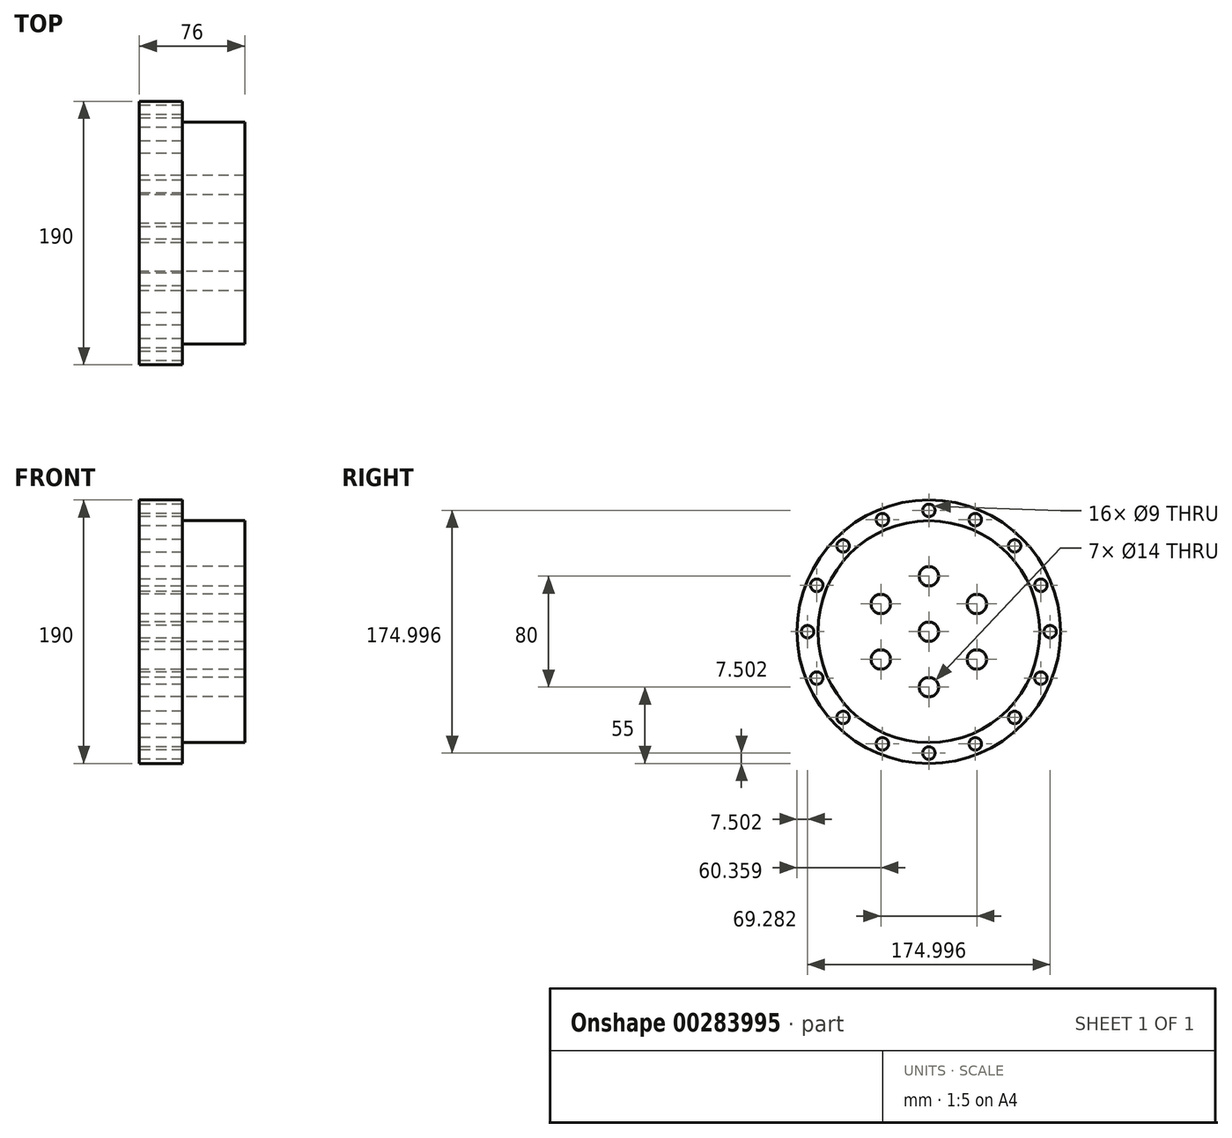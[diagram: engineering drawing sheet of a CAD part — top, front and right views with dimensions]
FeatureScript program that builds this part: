
annotation { "Feature Type Name" : "Feature", "Feature Type Description" : "" }
export const myFeature = defineFeature(function(context is Context, id is Id, definition is map)
    precondition{}
    {
        {
            var Q0;
            Q0=qCreatedBy(makeId("Right.planeOp"),FACE);
            var sketch = newSketch(context, id + "F0", { "sketchPlane" : qUnion([Q0])});
            skCircle(sketch, "E0", {"center": v(0, 0) * mm, "radius": 95 * mm});
            skCircle(sketch, "E1", {"center": v(0, 0) * mm, "radius": 80 * mm});
            skCircle(sketch, "E2", {"center": v(0, 0) * mm, "radius": 7 * mm});
            skCircle(sketch, "E3", {"center": v(0, 40) * mm, "radius": 7 * mm});
            skCircle(sketch, "E4.1.0", {"center": v(-34.64, 20) * mm, "radius": 7 * mm});
            skCircle(sketch, "E4.2.0", {"center": v(-34.64, -20) * mm, "radius": 7 * mm});
            skCircle(sketch, "E4.3.0", {"center": v(0, -40) * mm, "radius": 7 * mm});
            skCircle(sketch, "E4.4.0", {"center": v(34.64, -20) * mm, "radius": 7 * mm});
            skCircle(sketch, "E4.5.0", {"center": v(34.64, 20) * mm, "radius": 7 * mm});
            skCircle(sketch, "E5", {"center": v(0, 87.5) * mm, "radius": 4.5 * mm});
            skCircle(sketch, "E6.1.0", {"center": v(-33.48, 80.84) * mm, "radius": 4.5 * mm});
            skCircle(sketch, "E6.2.0", {"center": v(-61.87, 61.87) * mm, "radius": 4.5 * mm});
            skCircle(sketch, "E6.3.0", {"center": v(-80.84, 33.48) * mm, "radius": 4.5 * mm});
            skCircle(sketch, "E6.4.0", {"center": v(-87.5, 0) * mm, "radius": 4.5 * mm});
            skCircle(sketch, "E6.5.0", {"center": v(-80.84, -33.48) * mm, "radius": 4.5 * mm});
            skCircle(sketch, "E6.6.0", {"center": v(-61.87, -61.87) * mm, "radius": 4.5 * mm});
            skCircle(sketch, "E6.7.0", {"center": v(-33.48, -80.84) * mm, "radius": 4.5 * mm});
            skCircle(sketch, "E6.8.0", {"center": v(0, -87.5) * mm, "radius": 4.5 * mm});
            skCircle(sketch, "E6.9.0", {"center": v(33.48, -80.84) * mm, "radius": 4.5 * mm});
            skCircle(sketch, "E6.10.0", {"center": v(61.87, -61.87) * mm, "radius": 4.5 * mm});
            skCircle(sketch, "E6.11.0", {"center": v(80.84, -33.48) * mm, "radius": 4.5 * mm});
            skCircle(sketch, "E6.12.0", {"center": v(87.5, 0) * mm, "radius": 4.5 * mm});
            skCircle(sketch, "E6.13.0", {"center": v(80.84, 33.48) * mm, "radius": 4.5 * mm});
            skCircle(sketch, "E6.14.0", {"center": v(61.87, 61.87) * mm, "radius": 4.5 * mm});
            skCircle(sketch, "E6.15.0", {"center": v(33.48, 80.84) * mm, "radius": 4.5 * mm});
            skSolve(sketch);
        }
        {
            var Q0;
            Q0=makeQuery(id+"F0.imprint","IMPRINT",FACE,{"disambiguationData":[TD([[makeQuery(id+"F0.imprint","IMPRINT",EDGE,{"derivedFrom":sQuery(id+"F0.wireOp",EDGE,"E1")}),1.0]])]});
            extrude(context, id + "F1", {"entities" : qUnion([Q0]), "depth" : 76 * mm});
        }
        {
            var Q0;
            Q0=makeQuery(id+"F0.imprint","IMPRINT",FACE,{"disambiguationData":[TD([[makeQuery(id+"F0.imprint","IMPRINT",EDGE,{"derivedFrom":sQuery(id+"F0.wireOp",EDGE,"E0")}),1.0]])]});
            extrude(context, id + "F2", {"entities" : qUnion([Q0]), "operationType" : NewBodyOperationType.ADD, "depth" : 31 * mm});
        }
    });
